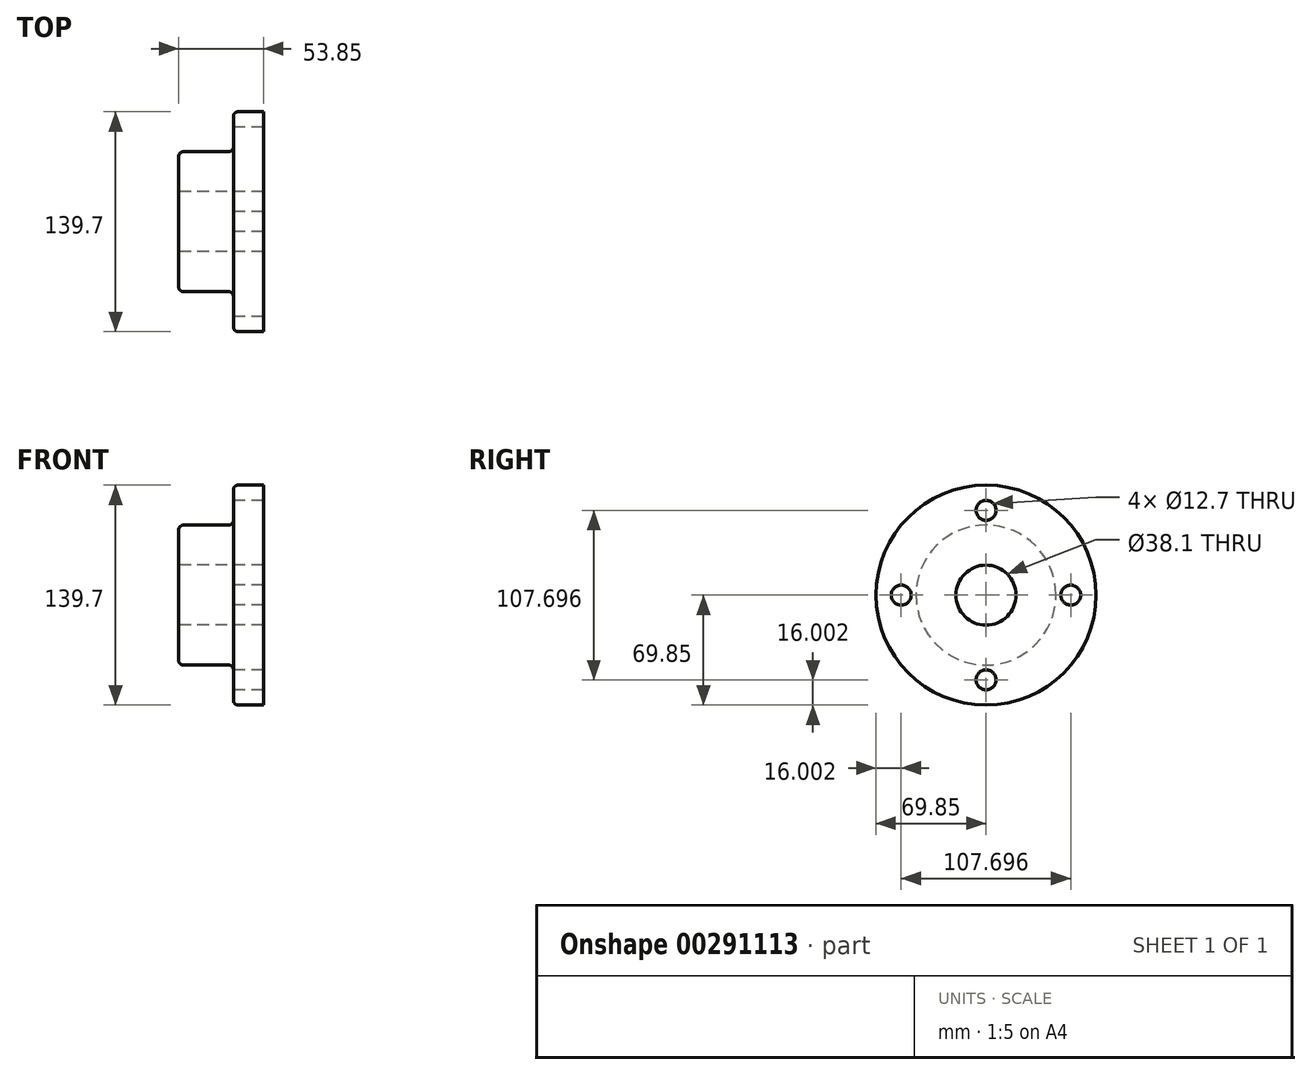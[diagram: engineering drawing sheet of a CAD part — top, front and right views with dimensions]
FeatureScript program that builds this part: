
annotation { "Feature Type Name" : "Feature", "Feature Type Description" : "" }
export const myFeature = defineFeature(function(context is Context, id is Id, definition is map)
    precondition{}
    {
        {
            var Q0;
            Q0=qCreatedBy(makeId("Front.planeOp"),FACE);
            var sketch = newSketch(context, id + "F0", { "sketchPlane" : qUnion([Q0])});
            skLineSegment(sketch, "E0", {"start": v(0, 0) * mm, "end": v(91.43, 0) * mm, "construction": true});
            skLineSegment(sketch, "E1", {"start": v(0, 19.05) * mm, "end": v(53.85, 19.05) * mm});
            skLineSegment(sketch, "E2", {"start": v(53.85, 19.05) * mm, "end": v(53.85, 69.85) * mm});
            skLineSegment(sketch, "E3", {"start": v(53.85, 69.85) * mm, "end": v(34.8, 69.85) * mm});
            skLineSegment(sketch, "E4", {"start": v(34.8, 69.85) * mm, "end": v(34.8, 44.45) * mm});
            skLineSegment(sketch, "E5", {"start": v(34.8, 44.45) * mm, "end": v(0, 44.45) * mm});
            skLineSegment(sketch, "E6", {"start": v(0, 44.45) * mm, "end": v(0, 19.05) * mm});
            skSolve(sketch);
        }
        {
            var Q0;
            Q0 = qSketchRegion(id + "F0", true);
            var Q1;
            Q1=sQuery(id+"F0.wireOp",EDGE,"E0");
            revolve(context, id + "F1", {"entities" : qUnion([Q0]), "axis" : qUnion([Q1]), "revolveType" : RevolveType.FULL});
        }
        {
            var Q0;
            Q0=qCreatedBy(makeId("Right.planeOp"),FACE);
            var sketch = newSketch(context, id + "F2", { "sketchPlane" : qUnion([Q0])});
            skCircle(sketch, "E7", {"center": v(0, 53.85) * mm, "radius": 6.35 * mm});
            skCircle(sketch, "E8", {"center": v(0, 0) * mm, "radius": 53.85 * mm, "construction": true});
            skCircle(sketch, "E9", {"center": v(53.85, 0) * mm, "radius": 6.35 * mm});
            skCircle(sketch, "E10", {"center": v(-53.85, 0) * mm, "radius": 6.35 * mm});
            skCircle(sketch, "E11", {"center": v(0, -53.85) * mm, "radius": 6.35 * mm});
            skSolve(sketch);
        }
        {
            var Q0;
            Q0 = qSketchRegion(id + "F2", true);
            extrude(context, id + "F3", {"entities" : qUnion([Q0]), "operationType" : NewBodyOperationType.REMOVE, "endBound" : BoundingType.THROUGH_ALL, "depth" : 25.4 * mm});
        }
        {
            var Q0;
            Q0=makeQuery(id+"F1.opRevolve","SWEPT_EDGE",EDGE,{"disambiguationData":[OSD([sQuery(id+"F0.wireOp",EDGE,"E4"),sQuery(id+"F0.wireOp",EDGE,"E5")])]});
            fillet(context, id + "F4", {"entities" : qUnion([Q0]), "radius" : 3.05 * mm, "tangentPropagation" : true, "allowEdgeOverflow" : false});
        }
        {
            var Q0;
            Q0=makeQuery(id+"F1.opRevolve","SWEPT_EDGE",EDGE,{"disambiguationData":[OSD([sQuery(id+"F0.wireOp",EDGE,"E5"),sQuery(id+"F0.wireOp",EDGE,"E6")])]});
            var Q1;
            Q1=makeQuery(id+"F1.opRevolve","SWEPT_EDGE",EDGE,{"disambiguationData":[OSD([sQuery(id+"F0.wireOp",EDGE,"E3"),sQuery(id+"F0.wireOp",EDGE,"E4")])]});
            fillet(context, id + "F5", {"entities" : qUnion([Q0, Q1]), "radius" : 3.05 * mm, "tangentPropagation" : true, "allowEdgeOverflow" : false});
        }
    });
